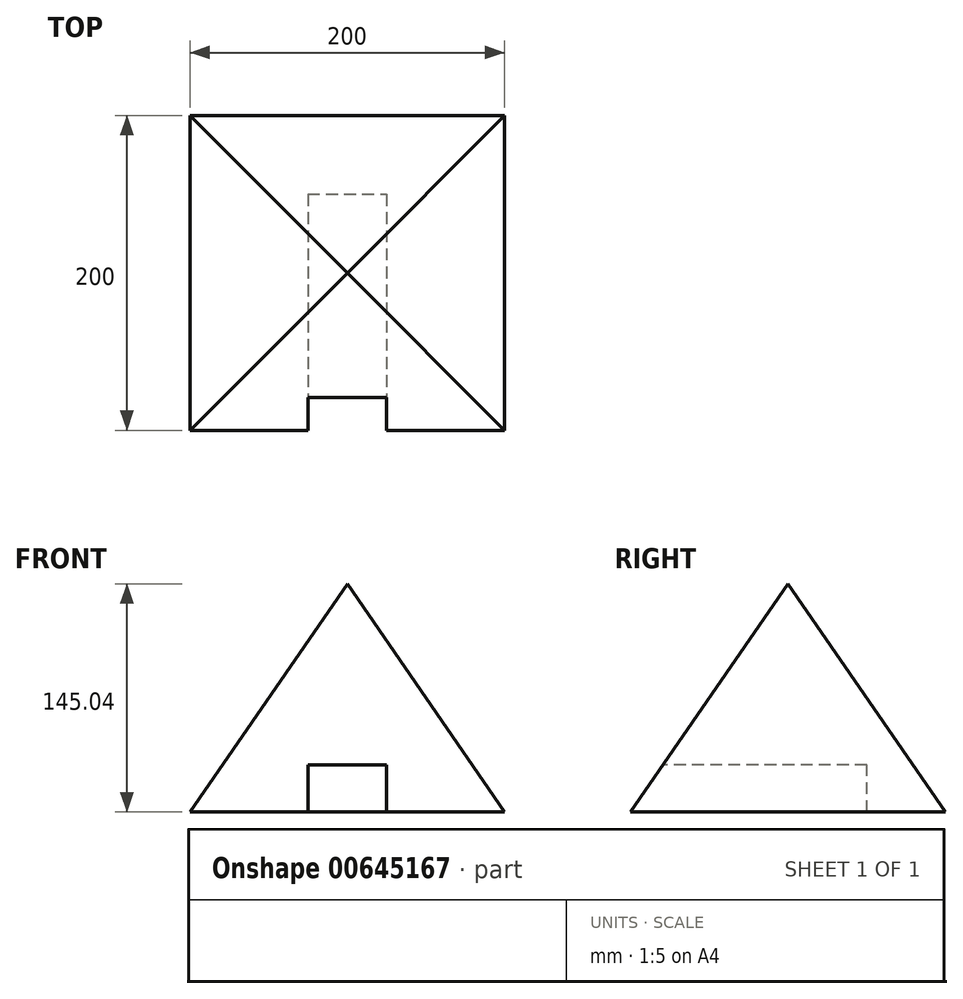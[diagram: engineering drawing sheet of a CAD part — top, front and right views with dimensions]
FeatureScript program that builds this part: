
annotation { "Feature Type Name" : "Feature", "Feature Type Description" : "" }
export const myFeature = defineFeature(function(context is Context, id is Id, definition is map)
    precondition{}
    {
        {
            var Q0;
            Q0=qCreatedBy(makeId("Top.planeOp"),FACE);
            var sketch = newSketch(context, id + "F0", { "sketchPlane" : qUnion([Q0])});
            skLineSegment(sketch, "E0.bottom", {"start": v(-100, -100) * mm, "end": v(100, -100) * mm});
            skLineSegment(sketch, "E0.top", {"start": v(-100, 100) * mm, "end": v(100, 100) * mm});
            skLineSegment(sketch, "E0.left", {"start": v(-100, -100) * mm, "end": v(-100, 100) * mm});
            skLineSegment(sketch, "E0.right", {"start": v(100, -100) * mm, "end": v(100, 100) * mm});
            skPoint(sketch, "E0.middle", {"position": v(0, 0) * mm});
            skSolve(sketch);
        }
        {
            var Q0;
            Q0=qCreatedBy(makeId("Front.planeOp"),FACE);
            var sketch = newSketch(context, id + "F1", { "sketchPlane" : qUnion([Q0])});
            skLineSegment(sketch, "E1", {"start": v(0, -4.96) * mm, "end": v(0, 145.04) * mm});
            skSolve(sketch);
        }
        {
            var Q0;
            Q0 = qSketchRegion(id + "F0", true);
            var Q1;
            Q1=sQuery(id+"F1.wireOp",VERTEX,"E1.end");
            loft(context, id + "F2", {"sheetProfilesArray" : [{ "sheetProfileEntities" : qUnion([Q0]) }, { "sheetProfileEntities" : qUnion([Q1]) }]});
        }
        {
            var Q0;
            Q0=qCreatedBy(makeId("Front.planeOp"),FACE);
            cPlane(context, id + "F3", {"entities" : qUnion([Q0]), "cplaneType" : CPlaneType.OFFSET, "offset" : 100 * mm, "width" : 150 * mm, "height" : 150 * mm});
        }
        {
            var Q0;
            Q0=qCreatedBy(id+"F3.planeOp",FACE);
            var sketch = newSketch(context, id + "F4", { "sketchPlane" : qUnion([Q0])});
            skLineSegment(sketch, "E2", {"start": v(-25, 0) * mm, "end": v(-25, 30) * mm});
            skLineSegment(sketch, "E3", {"start": v(-25, 30) * mm, "end": v(0, 30) * mm});
            skLineSegment(sketch, "E4.MirrorCS", {"start": v(25, 0) * mm, "end": v(25, 30) * mm});
            skLineSegment(sketch, "E5.MirrorCS", {"start": v(25, 30) * mm, "end": v(0, 30) * mm});
            skLineSegment(sketch, "E6", {"start": v(-25, 0) * mm, "end": v(25, 0) * mm});
            skSolve(sketch);
        }
        {
            var Q0;
            Q0 = qSketchRegion(id + "F4", true);
            extrude(context, id + "F5", {"entities" : qUnion([Q0]), "operationType" : NewBodyOperationType.REMOVE, "oppositeDirection" : true, "depth" : 150 * mm, "offsetDistance" : 25 * mm});
        }
    });
